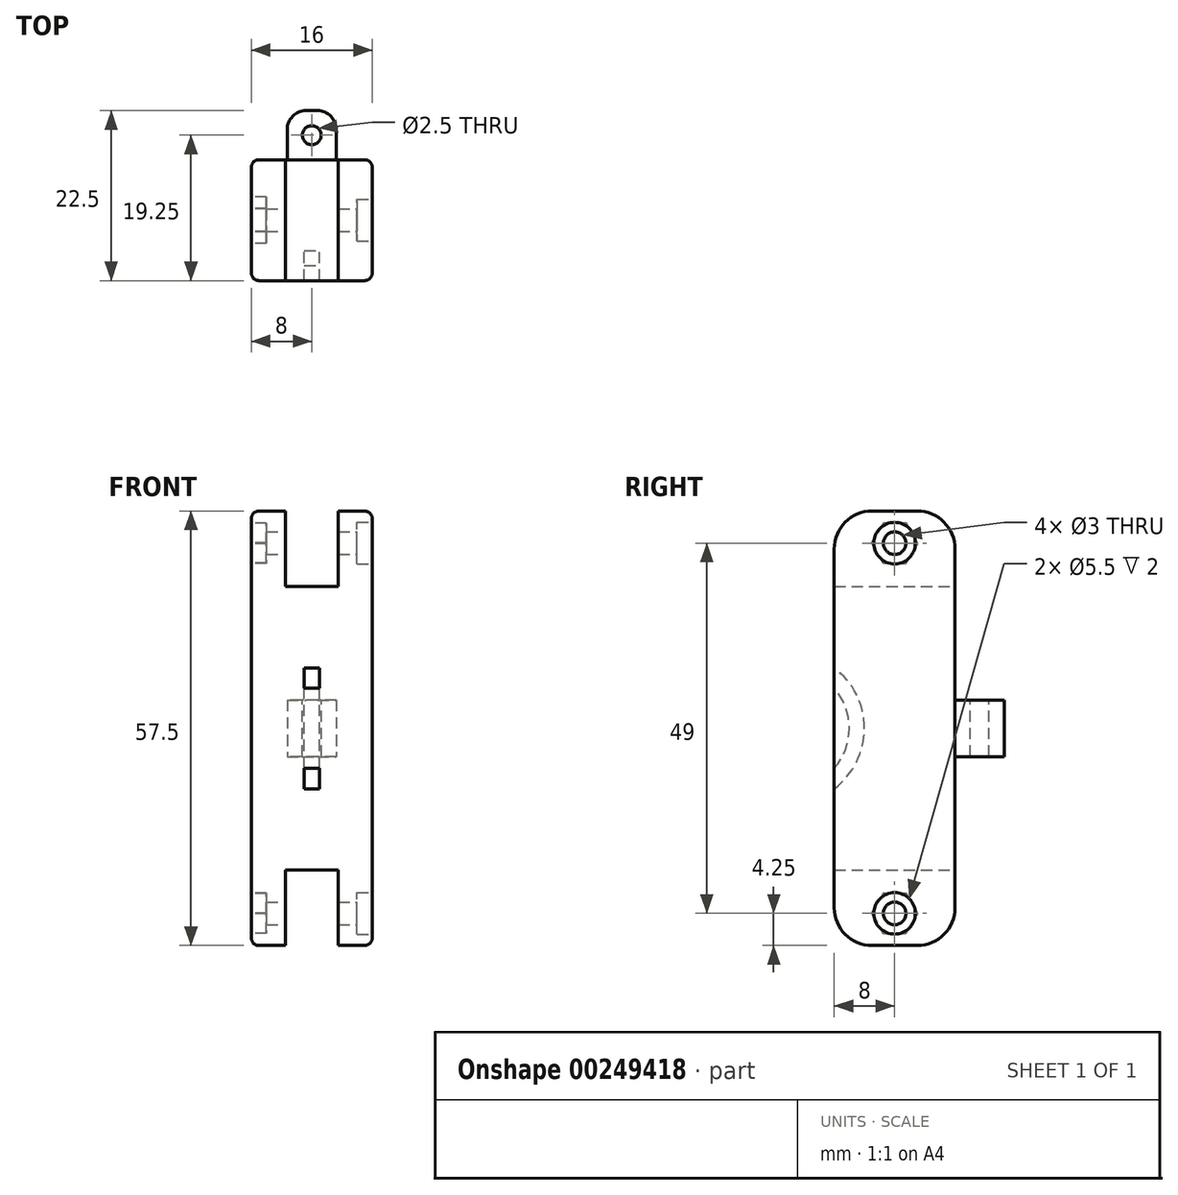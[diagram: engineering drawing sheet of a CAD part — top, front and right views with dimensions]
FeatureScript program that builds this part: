
annotation { "Feature Type Name" : "Feature", "Feature Type Description" : "" }
export const myFeature = defineFeature(function(context is Context, id is Id, definition is map)
    precondition{}
    {
        {
            var Q0;
            Q0=qCreatedBy(makeId("Front.planeOp"),FACE);
            var sketch = newSketch(context, id + "F0", { "sketchPlane" : qUnion([Q0])});
            skLineSegment(sketch, "E0.bottom", {"start": v(8, -28.75) * mm, "end": v(-8, -28.75) * mm});
            skLineSegment(sketch, "E0.top", {"start": v(8, 28.75) * mm, "end": v(-8, 28.75) * mm});
            skLineSegment(sketch, "E0.left", {"start": v(8, -28.75) * mm, "end": v(8, 28.75) * mm});
            skLineSegment(sketch, "E0.right", {"start": v(-8, -28.75) * mm, "end": v(-8, 28.75) * mm});
            skPoint(sketch, "E0.middle", {"position": v(0, 0) * mm});
            skLineSegment(sketch, "E1.top", {"start": v(-3.5, -18.75) * mm, "end": v(3.5, -18.75) * mm});
            skLineSegment(sketch, "E1.left", {"start": v(-3.5, -28.75) * mm, "end": v(-3.5, -18.75) * mm});
            skLineSegment(sketch, "E1.right", {"start": v(3.5, -28.75) * mm, "end": v(3.5, -18.75) * mm});
            skLineSegment(sketch, "E2.bottom", {"start": v(-3.5, 28.75) * mm, "end": v(3.5, 28.75) * mm});
            skLineSegment(sketch, "E2.top", {"start": v(-3.5, 18.75) * mm, "end": v(3.5, 18.75) * mm});
            skLineSegment(sketch, "E2.left", {"start": v(-3.5, 28.75) * mm, "end": v(-3.5, 18.75) * mm});
            skLineSegment(sketch, "E2.right", {"start": v(3.5, 28.75) * mm, "end": v(3.5, 18.75) * mm});
            skPoint(sketch, "E3", {"position": v(0, 23) * mm});
            skPoint(sketch, "E4", {"position": v(0, -26) * mm});
            skPoint(sketch, "E5", {"position": v(0, 18.75) * mm});
            skLineSegment(sketch, "E6", {"start": v(-3.5, -28.75) * mm, "end": v(3.5, -28.75) * mm});
            skLineSegment(sketch, "E7.bottom", {"start": v(3.25, 3.75) * mm, "end": v(-3.25, 3.75) * mm});
            skLineSegment(sketch, "E7.top", {"start": v(3.25, -3.75) * mm, "end": v(-3.25, -3.75) * mm});
            skLineSegment(sketch, "E7.left", {"start": v(3.25, 3.75) * mm, "end": v(3.25, -3.75) * mm});
            skLineSegment(sketch, "E7.right", {"start": v(-3.25, 3.75) * mm, "end": v(-3.25, -3.75) * mm});
            skSolve(sketch);
        }
        {
            var Q0;
            {var subQ1=sQuery(id+"F0.wireOp",EDGE,"E0.left");Q0=makeQuery(id+"F0.imprint","IMPRINT",FACE,{"disambiguationData":[TD([[makeQuery(id+"F0.imprint","IMPRINT",EDGE,{"derivedFrom":subQ1}),1.0]])]});}
            extrude(context, id + "F1", {"entities" : qUnion([Q0]), "depth" : 16 * mm, "symmetric" : true});
        }
        {
            var Q0;
            Q0=makeQuery(id+"F1.opExtrude","SWEPT_FACE",FACE,{"disambiguationData":[OSD([sQuery(id+"F0.wireOp",EDGE,"E0.left")])]});
            var sketch = newSketch(context, id + "F2", { "sketchPlane" : qUnion([Q0])});
            skLineSegment(sketch, "E8", {"start": v(0, 28.75) * mm, "end": v(0, 24.5) * mm});
            skPoint(sketch, "E8.endSnap0", {"position": v(0, 28.75) * mm});
            skLineSegment(sketch, "E9", {"start": v(0, -28.75) * mm, "end": v(0, -24.5) * mm});
            skPoint(sketch, "E9.endSnap0", {"position": v(0, -28.75) * mm});
            skCircle(sketch, "E10", {"center": v(0, 24.5) * mm, "radius": 2.75 * mm});
            skCircle(sketch, "E11", {"center": v(0, -24.5) * mm, "radius": 2.75 * mm});
            skCircle(sketch, "E12", {"center": v(0, 24.5) * mm, "radius": 1.5 * mm});
            skCircle(sketch, "E13", {"center": v(0, -24.5) * mm, "radius": 1.5 * mm});
            skSolve(sketch);
        }
        {
            var Q0;
            Q0=makeQuery(id+"F2.imprint","IMPRINT",FACE,{"disambiguationData":[TD([[makeQuery(id+"F2.imprint","IMPRINT",EDGE,{"derivedFrom":sQuery(id+"F2.wireOp",EDGE,"E10")}),1.0]])]});
            var Q1;
            Q1=makeQuery(id+"F2.imprint","IMPRINT",FACE,{"disambiguationData":[TD([[makeQuery(id+"F2.imprint","IMPRINT",EDGE,{"derivedFrom":sQuery(id+"F2.wireOp",EDGE,"E11")}),1.0]])]});
            extrude(context, id + "F3", {"entities" : qUnion([Q0, Q1]), "operationType" : NewBodyOperationType.REMOVE, "oppositeDirection" : true, "depth" : 2 * mm});
        }
        {
            var Q0;
            Q0=makeQuery(id+"F3.boolean.opBoolean","SPLIT",FACE,{"disambiguationData":[TD([makeQuery(id+"F3.opExtrude","SWEPT_FACE",FACE,{"disambiguationData":[OSD([sQuery(id+"F2.wireOp",EDGE,"E12")])]})])],"derivedFrom":makeQuery(id+"F1.opExtrude","SWEPT_FACE",FACE,{"disambiguationData":[OSD([sQuery(id+"F0.wireOp",EDGE,"E0.left")])]})});
            var Q1;
            Q1=makeQuery(id+"F3.boolean.opBoolean","SPLIT",FACE,{"disambiguationData":[TD([makeQuery(id+"F3.opExtrude","SWEPT_FACE",FACE,{"disambiguationData":[OSD([sQuery(id+"F2.wireOp",EDGE,"E13")])]})])],"derivedFrom":makeQuery(id+"F1.opExtrude","SWEPT_FACE",FACE,{"disambiguationData":[OSD([sQuery(id+"F0.wireOp",EDGE,"E0.left")])]})});
            extrude(context, id + "F4", {"entities" : qUnion([Q0, Q1]), "operationType" : NewBodyOperationType.REMOVE, "oppositeDirection" : true, "depth" : 25 * mm});
        }
        {
            var Q0;
            Q0=makeQuery(id+"F1.opExtrude","SWEPT_FACE",FACE,{"disambiguationData":[OSD([sQuery(id+"F0.wireOp",EDGE,"E0.right")])]});
            var sketch = newSketch(context, id + "F5", { "sketchPlane" : qUnion([Q0])});
            skLineSegment(sketch, "E14", {"start": v(0, 28.75) * mm, "end": v(0, 24.5) * mm});
            skLineSegment(sketch, "E15", {"start": v(0, -28.75) * mm, "end": v(0, -24.5) * mm});
            skCircle(sketch, "E16.cCircle", {"center": v(0, 24.5) * mm, "radius": 2.65 * mm, "construction": true});
            skLineSegment(sketch, "E16.0", {"start": v(3.06, 24.55) * mm, "end": v(1.57, 21.88) * mm});
            skLineSegment(sketch, "E16.1", {"start": v(1.57, 21.88) * mm, "end": v(-1.49, 21.83) * mm});
            skLineSegment(sketch, "E16.2", {"start": v(-1.49, 21.83) * mm, "end": v(-3.06, 24.45) * mm});
            skLineSegment(sketch, "E16.3", {"start": v(-3.06, 24.45) * mm, "end": v(-1.57, 27.12) * mm});
            skLineSegment(sketch, "E16.4", {"start": v(-1.57, 27.12) * mm, "end": v(1.49, 27.17) * mm});
            skLineSegment(sketch, "E16.5", {"start": v(1.49, 27.17) * mm, "end": v(3.06, 24.55) * mm});
            skPoint(sketch, "E16.0.midPoint", {"position": v(2.32, 23.21) * mm});
            skCircle(sketch, "E17.cCircle", {"center": v(0, -24.5) * mm, "radius": 2.65 * mm, "construction": true});
            skLineSegment(sketch, "E17.0", {"start": v(1.5, -21.83) * mm, "end": v(3.06, -24.46) * mm});
            skLineSegment(sketch, "E17.1", {"start": v(3.06, -24.46) * mm, "end": v(1.56, -27.13) * mm});
            skLineSegment(sketch, "E17.2", {"start": v(1.56, -27.13) * mm, "end": v(-1.5, -27.17) * mm});
            skLineSegment(sketch, "E17.3", {"start": v(-1.5, -27.17) * mm, "end": v(-3.06, -24.54) * mm});
            skLineSegment(sketch, "E17.4", {"start": v(-3.06, -24.54) * mm, "end": v(-1.56, -21.87) * mm});
            skLineSegment(sketch, "E17.5", {"start": v(-1.56, -21.87) * mm, "end": v(1.5, -21.83) * mm});
            skPoint(sketch, "E17.0.midPoint", {"position": v(2.28, -23.15) * mm});
            skSolve(sketch);
        }
        {
            var Q0;
            {var subQ0=sQuery(id+"F5.wireOp",EDGE,"E16.0");Q0=makeQuery(id+"F5.imprint","IMPRINT",FACE,{"disambiguationData":[TD([[makeQuery(id+"F5.imprint","IMPRINT",EDGE,{"derivedFrom":subQ0}),-1.0]])]});}
            var Q1;
            Q1=makeQuery(id+"F5.imprint","IMPRINT",FACE,{"disambiguationData":[TD([[makeQuery(id+"F5.imprint","IMPRINT",EDGE,{"derivedFrom":sQuery(id+"F5.wireOp",EDGE,"E17.0")}),-1.0]])]});
            extrude(context, id + "F6", {"entities" : qUnion([Q0, Q1]), "operationType" : NewBodyOperationType.REMOVE, "oppositeDirection" : true, "depth" : 2 * mm});
        }
        {
            var Q0;
            {var subQ0=sQuery(id+"F0.wireOp",EDGE,"E0.top");Q0=makeQuery(id+"F1.opExtrude","CAP_EDGE",EDGE,{"disambiguationData":[OSD([subQ0]),TDD([makeQuery(id+"F0.imprint","IMPRINT",EDGE,{"disambiguationData":[TD([[makeQuery(id+"F0.imprint","INTERSECT",VERTEX,{"derivedFrom":[subQ0,sQuery(id+"F0.wireOp",EDGE,"E0.left")]}),-1.0]])],"derivedFrom":subQ0})])],"isStart":false});}
            var Q1;
            {var subQ0=sQuery(id+"F0.wireOp",EDGE,"E0.top");Q1=makeQuery(id+"F1.opExtrude","CAP_EDGE",EDGE,{"disambiguationData":[OSD([subQ0]),TDD([makeQuery(id+"F0.imprint","IMPRINT",EDGE,{"disambiguationData":[TD([[makeQuery(id+"F0.imprint","INTERSECT",VERTEX,{"derivedFrom":[subQ0,sQuery(id+"F0.wireOp",EDGE,"E0.left")]}),-1.0]])],"derivedFrom":subQ0})])],"isStart":true});}
            var Q2;
            {var subQ0=sQuery(id+"F0.wireOp",EDGE,"E0.top");Q2=makeQuery(id+"F1.opExtrude","CAP_EDGE",EDGE,{"disambiguationData":[OSD([subQ0]),TDD([makeQuery(id+"F0.imprint","IMPRINT",EDGE,{"disambiguationData":[TD([[makeQuery(id+"F0.imprint","INTERSECT",VERTEX,{"derivedFrom":[subQ0,sQuery(id+"F0.wireOp",EDGE,"E0.right")]}),1.0]])],"derivedFrom":subQ0})])],"isStart":true});}
            var Q3;
            {var subQ0=sQuery(id+"F0.wireOp",EDGE,"E0.top");Q3=makeQuery(id+"F1.opExtrude","CAP_EDGE",EDGE,{"disambiguationData":[OSD([subQ0]),TDD([makeQuery(id+"F0.imprint","IMPRINT",EDGE,{"disambiguationData":[TD([[makeQuery(id+"F0.imprint","INTERSECT",VERTEX,{"derivedFrom":[subQ0,sQuery(id+"F0.wireOp",EDGE,"E0.right")]}),1.0]])],"derivedFrom":subQ0})])],"isStart":false});}
            fillet(context, id + "F7", {"entities" : qUnion([Q0, Q1, Q2, Q3]), "radius" : 5 * mm, "tangentPropagation" : true, "allowEdgeOverflow" : false});
        }
        {
            var Q0;
            {var subQ0=sQuery(id+"F0.wireOp",EDGE,"E0.bottom");Q0=makeQuery(id+"F1.opExtrude","CAP_EDGE",EDGE,{"disambiguationData":[OSD([subQ0]),TDD([makeQuery(id+"F0.imprint","IMPRINT",EDGE,{"disambiguationData":[TD([[makeQuery(id+"F0.imprint","INTERSECT",VERTEX,{"derivedFrom":[subQ0,sQuery(id+"F0.wireOp",EDGE,"E0.left")]}),-1.0]])],"derivedFrom":subQ0})])],"isStart":true});}
            var Q1;
            {var subQ0=sQuery(id+"F0.wireOp",EDGE,"E0.bottom");Q1=makeQuery(id+"F1.opExtrude","CAP_EDGE",EDGE,{"disambiguationData":[OSD([subQ0]),TDD([makeQuery(id+"F0.imprint","IMPRINT",EDGE,{"disambiguationData":[TD([[makeQuery(id+"F0.imprint","INTERSECT",VERTEX,{"derivedFrom":[subQ0,sQuery(id+"F0.wireOp",EDGE,"E0.right")]}),1.0]])],"derivedFrom":subQ0})])],"isStart":true});}
            var Q2;
            {var subQ0=sQuery(id+"F0.wireOp",EDGE,"E0.bottom");Q2=makeQuery(id+"F1.opExtrude","CAP_EDGE",EDGE,{"disambiguationData":[OSD([subQ0]),TDD([makeQuery(id+"F0.imprint","IMPRINT",EDGE,{"disambiguationData":[TD([[makeQuery(id+"F0.imprint","INTERSECT",VERTEX,{"derivedFrom":[subQ0,sQuery(id+"F0.wireOp",EDGE,"E0.left")]}),-1.0]])],"derivedFrom":subQ0})])],"isStart":false});}
            var Q3;
            {var subQ0=sQuery(id+"F0.wireOp",EDGE,"E0.bottom");Q3=makeQuery(id+"F1.opExtrude","CAP_EDGE",EDGE,{"disambiguationData":[OSD([subQ0]),TDD([makeQuery(id+"F0.imprint","IMPRINT",EDGE,{"disambiguationData":[TD([[makeQuery(id+"F0.imprint","INTERSECT",VERTEX,{"derivedFrom":[subQ0,sQuery(id+"F0.wireOp",EDGE,"E0.right")]}),1.0]])],"derivedFrom":subQ0})])],"isStart":false});}
            fillet(context, id + "F8", {"entities" : qUnion([Q0, Q1, Q2, Q3]), "radius" : 5 * mm, "tangentPropagation" : true, "allowEdgeOverflow" : false});
        }
        {
            var Q0;
            Q0=makeQuery(id+"F1.opExtrude","CAP_EDGE",EDGE,{"disambiguationData":[OSD([sQuery(id+"F0.wireOp",EDGE,"E0.right")])],"isStart":false});
            var Q1;
            Q1=makeQuery(id+"F1.opExtrude","CAP_EDGE",EDGE,{"disambiguationData":[OSD([sQuery(id+"F0.wireOp",EDGE,"E0.left")])],"isStart":false});
            var Q2;
            Q2=makeQuery(id+"F1.opExtrude","CAP_EDGE",EDGE,{"disambiguationData":[OSD([sQuery(id+"F0.wireOp",EDGE,"E0.left")])],"isStart":true});
            var Q3;
            Q3=makeQuery(id+"F1.opExtrude","CAP_EDGE",EDGE,{"disambiguationData":[OSD([sQuery(id+"F0.wireOp",EDGE,"E0.right")])],"isStart":true});
            fillet(context, id + "F9", {"entities" : qUnion([Q0, Q1, Q2, Q3]), "radius" : 1 * mm, "tangentPropagation" : true, "allowEdgeOverflow" : false});
        }
        {
            var Q0;
            Q0=makeQuery(id+"F0.imprint","IMPRINT",FACE,{"disambiguationData":[TD([[makeQuery(id+"F0.imprint","IMPRINT",EDGE,{"derivedFrom":sQuery(id+"F0.wireOp",EDGE,"E7.bottom")}),1.0]])]});
            extrude(context, id + "F10", {"entities" : qUnion([Q0]), "operationType" : NewBodyOperationType.ADD, "depth" : 29 * mm, "symmetric" : true});
        }
        {
            var Q0;
            {var subQ0=sQuery(id+"F0.wireOp",EDGE,"E7.right");var subQ1=sQuery(id+"F0.wireOp",EDGE,"E7.left");var subQ2=sQuery(id+"F0.wireOp",EDGE,"E7.top");var subQ3=sQuery(id+"F0.wireOp",EDGE,"E7.bottom");Q0=makeQuery(id+"F10.boolean.opBoolean","SPLIT",FACE,{"disambiguationData":[TD([makeQuery(id+"F10.opExtrude","CAP_FACE",FACE,{"disambiguationData":[OSD([subQ3,subQ2,subQ1,subQ0])],"isStart":true})])],"derivedFrom":makeQuery(id+"F10.opExtrude","SWEPT_FACE",FACE,{"disambiguationData":[OSD([subQ3])]})});}
            var sketch = newSketch(context, id + "F11", { "sketchPlane" : qUnion([Q0])});
            skPoint(sketch, "E18", {"position": v(0, 11.25) * mm});
            skCircle(sketch, "E19", {"center": v(0, 11.25) * mm, "radius": 1.25 * mm});
            skCircle(sketch, "E20", {"center": v(0, -11.25) * mm, "radius": 1.25 * mm});
            skSolve(sketch);
        }
        {
            var Q0;
            Q0=makeQuery(id+"F11.imprint","IMPRINT",FACE,{"disambiguationData":[TD([[makeQuery(id+"F11.imprint","IMPRINT",EDGE,{"derivedFrom":sQuery(id+"F11.wireOp",EDGE,"E19")}),1.0]])]});
            var Q1;
            Q1=makeQuery(id+"F11.imprint","IMPRINT",FACE,{"disambiguationData":[TD([[makeQuery(id+"F11.imprint","IMPRINT",EDGE,{"derivedFrom":sQuery(id+"F11.wireOp",EDGE,"E20")}),1.0]])]});
            extrude(context, id + "F12", {"entities" : qUnion([Q0, Q1]), "operationType" : NewBodyOperationType.REMOVE, "endBound" : BoundingType.THROUGH_ALL, "oppositeDirection" : true, "depth" : 25 * mm});
        }
        {
            var Q0;
            Q0=makeQuery(id+"F10.opExtrude","CAP_EDGE",EDGE,{"disambiguationData":[OSD([sQuery(id+"F0.wireOp",EDGE,"E7.right")])],"isStart":true});
            var Q1;
            Q1=makeQuery(id+"F10.opExtrude","CAP_EDGE",EDGE,{"disambiguationData":[OSD([sQuery(id+"F0.wireOp",EDGE,"E7.left")])],"isStart":true});
            var Q2;
            Q2=makeQuery(id+"F10.opExtrude","CAP_EDGE",EDGE,{"disambiguationData":[OSD([sQuery(id+"F0.wireOp",EDGE,"E7.right")])],"isStart":false});
            var Q3;
            Q3=makeQuery(id+"F10.opExtrude","CAP_EDGE",EDGE,{"disambiguationData":[OSD([sQuery(id+"F0.wireOp",EDGE,"E7.left")])],"isStart":false});
            fillet(context, id + "F13", {"entities" : qUnion([Q0, Q1, Q2, Q3]), "radius" : 2.5 * mm, "tangentPropagation" : true, "allowEdgeOverflow" : false});
        }
        {
            var Q0;
            {var subQ0=sQuery(id+"F0.wireOp",EDGE,"E7.right");var subQ1=sQuery(id+"F0.wireOp",EDGE,"E7.left");var subQ2=sQuery(id+"F0.wireOp",EDGE,"E7.top");var subQ3=sQuery(id+"F0.wireOp",EDGE,"E7.bottom");Q0=makeQuery(id+"F10.boolean.opBoolean","SPLIT",FACE,{"disambiguationData":[TD([makeQuery(id+"F10.opExtrude","CAP_FACE",FACE,{"disambiguationData":[OSD([subQ3,subQ2,subQ1,subQ0])],"isStart":false})])],"derivedFrom":makeQuery(id+"F10.opExtrude","SWEPT_FACE",FACE,{"disambiguationData":[OSD([subQ3])]})});}
            var sketch = newSketch(context, id + "F14", { "sketchPlane" : qUnion([Q0])});
            skLineSegment(sketch, "E21.0.0", {"start": v(-0.75, -14.5) * mm, "end": v(0.75, -14.5) * mm});
            skArc(sketch, "E21.0.1", {"start": v(0.75, -14.5) * mm, "mid": v(2.52, -13.77) * mm, "end": v(3.25, -12) * mm});
            skLineSegment(sketch, "E21.0.2", {"start": v(3.25, -12) * mm, "end": v(3.25, -8) * mm});
            skLineSegment(sketch, "E21.0.3", {"start": v(3.25, -8) * mm, "end": v(-3.25, -8) * mm});
            skLineSegment(sketch, "E21.0.4", {"start": v(-3.25, -8) * mm, "end": v(-3.25, -12) * mm});
            skArc(sketch, "E21.0.5", {"start": v(-3.25, -12) * mm, "mid": v(-2.52, -13.77) * mm, "end": v(-0.75, -14.5) * mm});
            skSolve(sketch);
        }
        {
            var Q0;
            Q0=makeQuery(id+"F14.imprint","IMPRINT",FACE,{"disambiguationData":[TD([[makeQuery(id+"F14.imprint","IMPRINT",EDGE,{"derivedFrom":sQuery(id+"F14.wireOp",EDGE,"E21.0.0")}),-1.0]])]});
            extrude(context, id + "F15", {"entities" : qUnion([Q0]), "operationType" : NewBodyOperationType.REMOVE, "endBound" : BoundingType.THROUGH_ALL, "oppositeDirection" : true, "depth" : 25 * mm});
        }
        {
            var Q0;
            Q0=qCreatedBy(makeId("Right.planeOp"),FACE);
            var sketch = newSketch(context, id + "F16", { "sketchPlane" : qUnion([Q0])});
            skLineSegment(sketch, "E22", {"start": v(-8, 18.75) * mm, "end": v(-8, 5.3) * mm});
            skArc(sketch, "E23", {"start": v(-8, -8) * mm, "mid": v(-4, 0) * mm, "end": v(-8, 8) * mm});
            skPoint(sketch, "E23.first.point", {"position": v(-8, -8) * mm});
            skPoint(sketch, "E23.second.point", {"position": v(-8, 8) * mm});
            skPoint(sketch, "E23.third.point", {"position": v(-24, 0) * mm});
            skArc(sketch, "E24", {"start": v(-8, -5.3) * mm, "mid": v(-6, 0) * mm, "end": v(-8, 5.3) * mm});
            skLineSegment(sketch, "E25", {"start": v(-8, 5.3) * mm, "end": v(-8, 8) * mm});
            skLineSegment(sketch, "E26", {"start": v(-8, -8) * mm, "end": v(-8, -5.3) * mm});
            skLineSegment(sketch, "E27.trimOffspring", {"start": v(-8, -5.3) * mm, "end": v(-8, -18.75) * mm});
            skSolve(sketch);
        }
        {
            var Q0;
            Q0 = qSketchRegion(id + "F16", true);
            extrude(context, id + "F17", {"entities" : qUnion([Q0]), "operationType" : NewBodyOperationType.REMOVE, "oppositeDirection" : true, "depth" : 2 * mm, "symmetric" : true});
        }
    });
